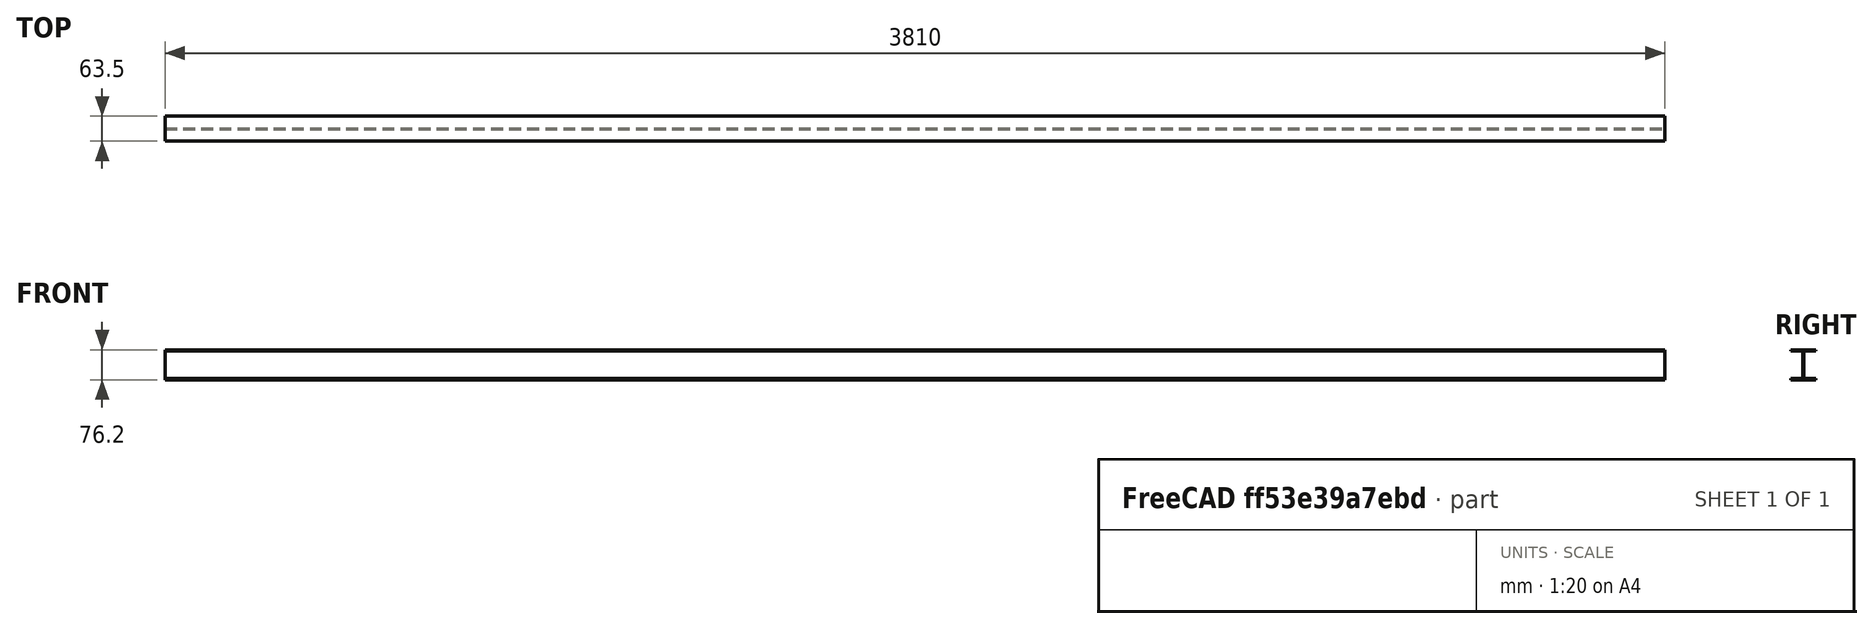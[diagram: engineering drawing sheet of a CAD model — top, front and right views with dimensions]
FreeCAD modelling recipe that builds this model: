
FCSTD DOCUMENT  (FreeCAD 0.18.1R)
Label: I-beam
License: All rights reserved
LicenseURL: http://en.wikipedia.org/wiki/All_rights_reserved
objects: PartDesign::Body×3, Sketcher::SketchObject×2, PartDesign::Pad×1, PartDesign::ShapeBinder×1
note: 8 computed .brp shape members not serialized (recipe doc carries the construction recipe); baked Part::Feature solids carry a one-line shape summary decoded from their .brp

FEATURE [Sketcher::SketchObject] Sketch
  MapMode = 5
  Placement = pos=(0,0,0) rot=(0.57735,0.57735,0.57735;2.0944rad)
  Support = -> [YZ_Plane001]
  sketch-geometry (12):
    g0: LineSegment StartX=-23.2257 StartY=-16.3716 StartZ=0 EndX=40.2743 EndY=-16.3716 EndZ=0
    g1: LineSegment StartX=40.2743 StartY=-16.3716 StartZ=0 EndX=40.2743 EndY=-13.0716 EndZ=0
    g2: LineSegment StartX=40.2743 StartY=-13.0716 StartZ=0 EndX=10.1743 EndY=-13.0716 EndZ=0
    g3: LineSegment StartX=10.1743 StartY=-13.0716 StartZ=0 EndX=10.1743 EndY=56.5284 EndZ=0
    g4: LineSegment StartX=10.1743 StartY=56.5284 StartZ=0 EndX=40.2743 EndY=56.5284 EndZ=0
    g5: LineSegment StartX=40.2743 StartY=56.5284 StartZ=0 EndX=40.2743 EndY=59.8284 EndZ=0
    g6: LineSegment StartX=40.2743 StartY=59.8284 StartZ=0 EndX=-23.2257 EndY=59.8284 EndZ=0
    g7: LineSegment StartX=-23.2257 StartY=59.8284 StartZ=0 EndX=-23.2257 EndY=56.5284 EndZ=0
    g8: LineSegment StartX=-23.2257 StartY=56.5284 StartZ=0 EndX=6.87433 EndY=56.5284 EndZ=0
    g9: LineSegment StartX=6.87433 StartY=56.5284 StartZ=0 EndX=6.87433 EndY=-13.0716 EndZ=0
    g10: LineSegment StartX=6.87433 StartY=-13.0716 StartZ=0 EndX=-23.2257 EndY=-13.0716 EndZ=0
    g11: LineSegment StartX=-23.2257 StartY=-13.0716 StartZ=0 EndX=-23.2257 EndY=-16.3716 EndZ=0
  constraints (33):
    c: Coincident(g0,g1)
    c: Coincident(g1,g2)
    c: Coincident(g2,g3)
    c: Coincident(g3,g4)
    c: Coincident(g4,g5)
    c: Coincident(g5,g6)
    c: Coincident(g6,g7)
    c: Coincident(g7,g8)
    c: Coincident(g8,g9)
    c: Coincident(g9,g10)
    c: Coincident(g10,g11)
    c: Coincident(g11,g0)
    c: Vertical(g11)
    c: Vertical(g1)
    c: Vertical(g3)
    c: Vertical(g9)
    c: Vertical(g5)
    c: Vertical(g7)
    c: Horizontal(g6)
    c: Horizontal(g8)
    c: Horizontal(g4)
    c: Horizontal(g0)
    c: Horizontal(g10)
    c: Horizontal(g2)
    c: DistanceX(g6,g6) = 63.5
    c: DistanceX(g8,g3) = 3.3
    c: DistanceY(g11,g11) = 3.3
    c: DistanceX(g8,g8) = 30.1
    c: DistanceY(g0,g5) = 76.2
    c: Equal(g7,g5)
    c: Equal(g11,g1)
    c: Equal(g0,g6)
    c: Equal(g8,g10)
FEATURE [PartDesign::Pad] Pad
  Length = 3810
  Length2 = 100
  Placement = pos=(0,0,0) rot=(0.57735,0.57735,0.57735;2.0944rad)
  Profile = -> Sketch
  Type = 0
FEATURE [PartDesign::Body] Body001
  Group = -> [Sketch,Pad]
  Origin = -> Origin001
  Tip = -> Pad
FEATURE [Sketcher::SketchObject] Sketch001
  MapMode = 5
  Placement = pos=(0,0,0) rot=(0.57735,0.57735,0.57735;2.0944rad)
  Support = -> [YZ_Plane]
  sketch-geometry (8):
    g0: LineSegment StartX=-134.133 StartY=43.7067 StartZ=0 EndX=-57.9332 EndY=43.7067 EndZ=0
    g1: LineSegment StartX=-134.133 StartY=43.7067 StartZ=0 EndX=-134.133 EndY=-7.09327 EndZ=0
    g2: LineSegment StartX=-134.133 StartY=-7.09327 StartZ=0 EndX=-57.9332 EndY=-7.09327 EndZ=0
    g3: LineSegment StartX=-57.9332 StartY=-7.09327 StartZ=0 EndX=-57.9332 EndY=43.7067 EndZ=0
    g4: LineSegment StartX=-130.833 StartY=40.4067 StartZ=0 EndX=-61.2332 EndY=40.4067 EndZ=0
    g5: LineSegment StartX=-61.2332 StartY=40.4067 StartZ=0 EndX=-61.2332 EndY=-3.79327 EndZ=0
    g6: LineSegment StartX=-61.2332 StartY=-3.79327 StartZ=0 EndX=-130.833 EndY=-3.79327 EndZ=0
    g7: LineSegment StartX=-130.833 StartY=-3.79327 StartZ=0 EndX=-130.833 EndY=40.4067 EndZ=0
  constraints (23):
    c: Vertical(g1)
    c: Horizontal(g0)
    c: Vertical(g3)
    c: Horizontal(g2)
    c: Equal(g0,g2)
    c: Equal(g3,g1)
    c: Coincident(g0,g3)
    c: Coincident(g3,g2)
    c: Coincident(g2,g1)
    c: DistanceX(g0,g0) = 76.2
    c: DistanceY(g1,g1) = 50.8
    c: Coincident(g4,g5)
    c: Coincident(g5,g6)
    c: Coincident(g6,g7)
    c: Coincident(g7,g4)
    c: Horizontal(g4)
    c: Horizontal(g6)
    c: Vertical(g5)
    c: Vertical(g7)
    c: DistanceX(g0,g4) = 3.3
    c: DistanceX(g4,g0) = 3.3
    c: DistanceY(g4,g0) = 3.3
    c: DistanceY(g2,g5) = 3.3
FEATURE [PartDesign::Body] Body
  Group = -> [Sketch001]
  Origin = -> Origin
FEATURE [PartDesign::ShapeBinder] ReferenceSketch001
  Placement = pos=(0,0,0) rot=(0.57735,0.57735,0.57735;2.0944rad)
  Support = -> [Sketch001]
  TraceSupport = false
FEATURE [PartDesign::Body] Body002
  Group = -> [ReferenceSketch001]
  Origin = -> Origin002
